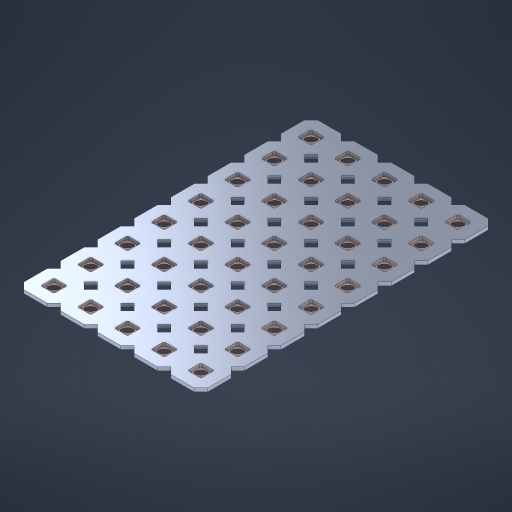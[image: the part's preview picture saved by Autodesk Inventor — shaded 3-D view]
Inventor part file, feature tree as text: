
AUTODESK INVENTOR PART (.ipt)
format: ipt  version: 2023 (Build 270158000, 158)  size: 730,624 bytes
history: native  units: in
note: dims shown in document units (in); Inventor stores cm internally (conversion verified against a paired STEP export)
features: other x41, extrude x39, sketch x2, pattern_linear x1
ambient origin geometry x8: Origin, YZ Plane, XZ Plane, XY Plane, X Axis, Y Axis, Z Axis, Center Point
bodies: Solid1 (feature_tree), Body (feature_tree)
feature tree (83):
  pattern_linear  "Rectangular Pattern1"  Spacing1=0.09in  [1 undecoded]
  sketch  "Sketch1"  dims[d1=0.5in]
  sketch  "Sketch2"  dims[d2=0.182in d3=0.09in d4=0.09in d5=0.09in d6=0.09in d7=0.09in d8=0.09in d9=0.09in d10=0.09in d11=0.02in d13=0.0in d14=0.172in d15=0.0625in d16=0.0in d19=0.5in d22=0.5in]
  other  "Srf1"
  other  "Srf126"
  other  "Srf127"
  other  "Srf128"
  other  "Srf129"
  other  "Srf130"
  other  "Srf131"
  other  "Srf250"
  other  "Srf268"
  other  "Srf269"
  other  "Srf270"
  other  "Srf271"
  other  "Srf272"
  other  "Srf273"
  other  "Srf274"
  other  "Srf275"
  other  "Srf293"
  other  "Srf294"
  other  "Srf295"
  other  "Srf296"
  other  "Srf297"
  other  "Srf298"
  other  "Srf299"
  other  "Srf300"
  other  "Srf318"
  other  "Srf319"
  other  "Srf320"
  other  "Srf321"
  other  "Srf322"
  other  "Srf323"
  other  "Srf324"
  other  "Srf325"
  other  "Srf343"
  other  "Srf344"
  other  "Srf345"
  other  "Srf346"
  other  "Srf347"
  other  "Srf348"
  other  "Srf349"
  other  "Srf350"
  other  "Circle"
  extrude  "ExtrusionSrf126"  Depth=0.09in
  extrude  "ExtrusionSrf127"  Depth=0.09in
  extrude  "ExtrusionSrf128"  Depth=0.09in
  extrude  "ExtrusionSrf129"  Depth=0.09in
  extrude  "ExtrusionSrf130"  Depth=0.09in
  extrude  "ExtrusionSrf131"  Depth=0.09in
  extrude  "ExtrusionSrf250"  Depth=0.09in
  extrude  "ExtrusionSrf268"  Depth=0.02in
  extrude  "ExtrusionSrf269"  TaperAngle=0.0deg  [1 undecoded]
  extrude  "ExtrusionSrf270"  Depth=0.5in
  extrude  "ExtrusionSrf271"  Depth=0.5in TaperAngle=0.0deg
  extrude  "ExtrusionSrf272"  Depth=0.5in
  extrude  "ExtrusionSrf273"  Depth=0.5in
  extrude  "ExtrusionSrf274"  [1 undecoded]
  extrude  "ExtrusionSrf275"  [1 undecoded]
  extrude  "ExtrusionSrf293"  [1 undecoded]
  extrude  "ExtrusionSrf294"  [1 undecoded]
  extrude  "ExtrusionSrf295"  [1 undecoded]
  extrude  "ExtrusionSrf296"  [1 undecoded]
  extrude  "ExtrusionSrf297"  [1 undecoded]
  extrude  "ExtrusionSrf298"  [1 undecoded]
  extrude  "ExtrusionSrf299"  [1 undecoded]
  extrude  "ExtrusionSrf300"  [1 undecoded]
  extrude  "ExtrusionSrf318"  [1 undecoded]
  extrude  "ExtrusionSrf319"  [1 undecoded]
  extrude  "ExtrusionSrf320"  [1 undecoded]
  extrude  "ExtrusionSrf321"  [1 undecoded]
  extrude  "ExtrusionSrf322"  [1 undecoded]
  extrude  "ExtrusionSrf323"  [1 undecoded]
  extrude  "ExtrusionSrf324"  [1 undecoded]
  extrude  "ExtrusionSrf325"  [1 undecoded]
  extrude  "ExtrusionSrf343"  [1 undecoded]
  extrude  "ExtrusionSrf344"  [1 undecoded]
  extrude  "ExtrusionSrf345"  [1 undecoded]
  extrude  "ExtrusionSrf346"  [1 undecoded]
  extrude  "ExtrusionSrf347"  [1 undecoded]
  extrude  "ExtrusionSrf348"  [1 undecoded]
  extrude  "ExtrusionSrf349"  [1 undecoded]
  extrude  "ExtrusionSrf350"  [1 undecoded]
note: 28 required parameter values undecoded (feature->parameter linkage not recoverable at this tier; creation-order binding heuristic only, values carry confidence <= 0.55)
